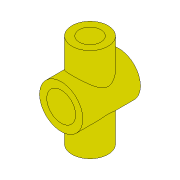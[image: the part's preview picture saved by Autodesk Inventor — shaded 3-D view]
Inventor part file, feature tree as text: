
AUTODESK INVENTOR PART (.ipt)
format: ipt  version: 2022.5 (Build 265521000, 521)  size: 146,432 bytes
history: native  units: mm
features: sketch x4, revolve x2, extrude x2
ambient origin geometry x8: Origin, YZ Plane, XZ Plane, XY Plane, X Axis, Y Axis, Z Axis, Center Point
bodies: Body1 (feature_tree)
feature tree (8):
  revolve  "Revolution1"  [1 undecoded]
  revolve  "Revolution2"  [1 undecoded]
  extrude  "Extrusion8"  Depth=16.0mm
  extrude  "Extrusion9"  Depth=12.0mm
  sketch  "Sketch8"  dims[d26=26.0mm d27=16.0mm]
  sketch  "Sketch9"  dims[d28=10.0mm d29=6.0mm]
  sketch  "Sketch10"  dims[d30=90.0deg d31=16.0mm]
  sketch  "Sketch11"  dims[d32=16.0mm d33=12.0mm d34=90.0deg d35=16.0mm d36=0.0mm d37=0.0mm d38=0.0mm d39=0.0mm]
note: 2 required parameter values undecoded (feature->parameter linkage not recoverable at this tier; creation-order binding heuristic only, values carry confidence <= 0.55)
